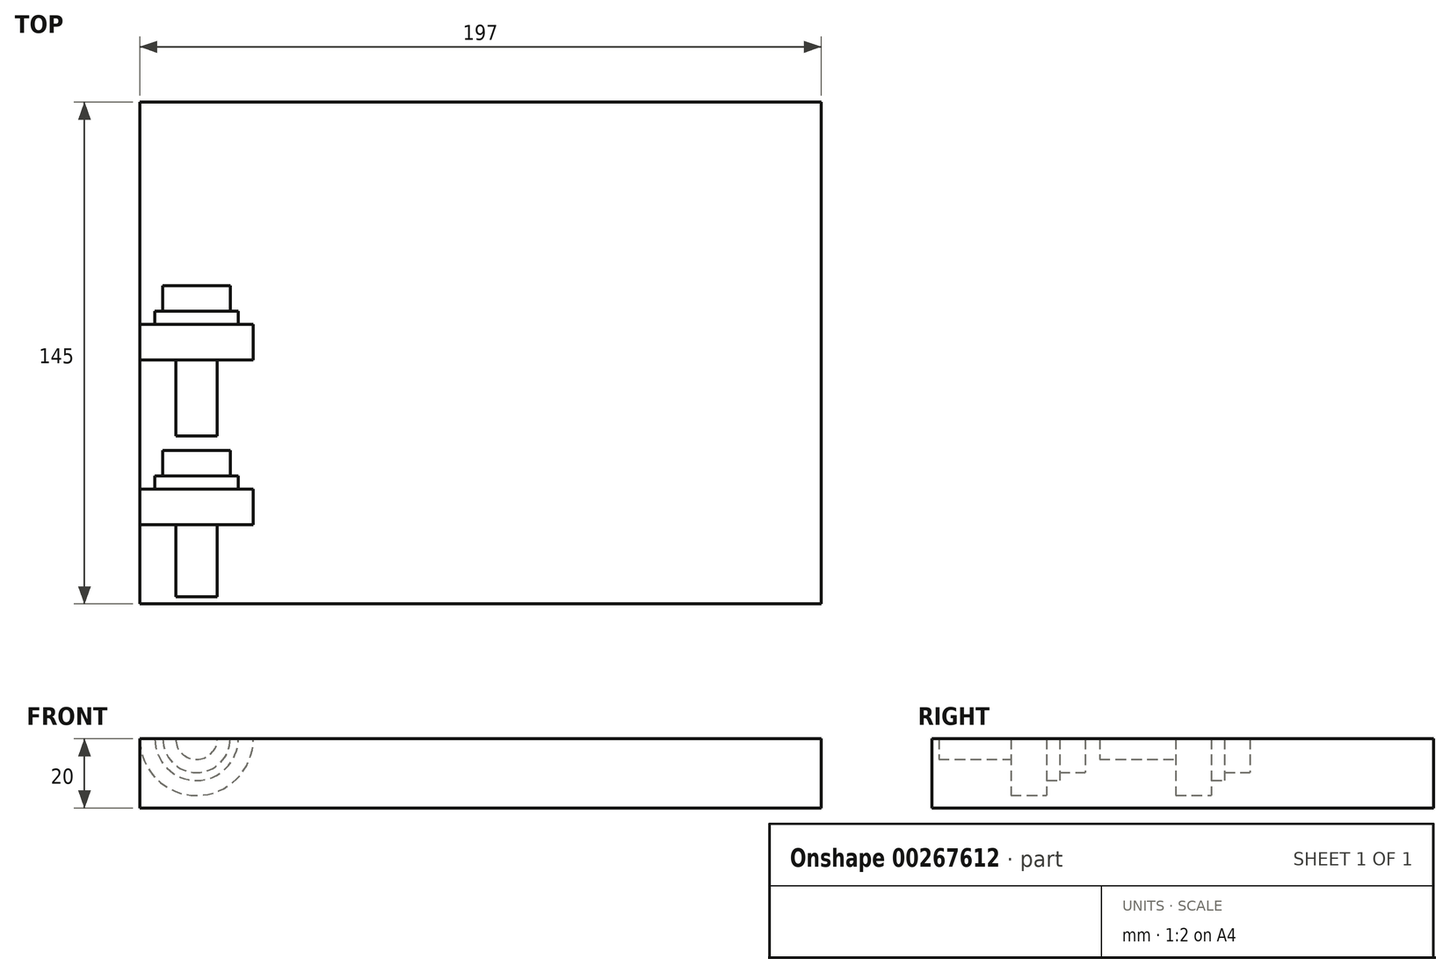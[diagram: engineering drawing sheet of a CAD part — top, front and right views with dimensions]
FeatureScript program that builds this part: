
annotation { "Feature Type Name" : "Feature", "Feature Type Description" : "" }
export const myFeature = defineFeature(function(context is Context, id is Id, definition is map)
    precondition{}
    {
        {
            var Q0;
            Q0=qCreatedBy(makeId("Top.planeOp"),FACE);
            var sketch = newSketch(context, id + "F0", { "sketchPlane" : qUnion([Q0])});
            skLineSegment(sketch, "E0.bottom", {"start": v(-40.2, 136.98) * mm, "end": v(156.8, 136.98) * mm});
            skLineSegment(sketch, "E0.top", {"start": v(-40.2, -8.02) * mm, "end": v(156.8, -8.02) * mm});
            skLineSegment(sketch, "E0.left", {"start": v(-40.2, 136.98) * mm, "end": v(-40.2, -8.02) * mm});
            skLineSegment(sketch, "E0.right", {"start": v(156.8, 136.98) * mm, "end": v(156.8, -8.02) * mm});
            skSolve(sketch);
        }
        {
            var Q0;
            Q0=makeQuery(id+"F0.imprint","IMPRINT",FACE,{"disambiguationData":[TD([[makeQuery(id+"F0.imprint","IMPRINT",EDGE,{"derivedFrom":sQuery(id+"F0.wireOp",EDGE,"E0.bottom")}),-1.0]])]});
            extrude(context, id + "F1", {"entities" : qUnion([Q0]), "depth" : 20 * mm});
        }
        {
            var Q0;
            Q0=makeQuery(id+"F1.opExtrude","CAP_FACE",FACE,{"disambiguationData":[OSD([sQuery(id+"F0.wireOp",EDGE,"E0.bottom"),sQuery(id+"F0.wireOp",EDGE,"E0.top"),sQuery(id+"F0.wireOp",EDGE,"E0.left"),sQuery(id+"F0.wireOp",EDGE,"E0.right")])],"isStart":false});
            var sketch = newSketch(context, id + "F2", { "sketchPlane" : qUnion([Q0])});
            skPoint(sketch, "E1.top.end.orphan", {"position": v(-29.8, 15.98) * mm});
            skPoint(sketch, "E2.top.start.orphan", {"position": v(-21.54, 15.98) * mm});
            skPoint(sketch, "E3.right.start.orphan", {"position": v(-38.04, 15.98) * mm});
            skLineSegment(sketch, "E4.bottom", {"start": v(-23.8, -6.02) * mm, "end": v(-29.8, -6.02) * mm});
            skLineSegment(sketch, "E4.top", {"start": v(-23.8, 14.8) * mm, "end": v(-29.8, 14.8) * mm});
            skLineSegment(sketch, "E4.left", {"start": v(-23.8, -6.02) * mm, "end": v(-23.8, 14.8) * mm});
            skLineSegment(sketch, "E4.right", {"start": v(-29.8, -6.02) * mm, "end": v(-29.8, 14.8) * mm});
            skLineSegment(sketch, "E5.bottom", {"start": v(-23.8, 14.8) * mm, "end": v(-40.2, 14.8) * mm});
            skLineSegment(sketch, "E5.top", {"start": v(-23.8, 25.1) * mm, "end": v(-40.2, 25.1) * mm});
            skLineSegment(sketch, "E5.left", {"start": v(-23.8, 14.8) * mm, "end": v(-23.8, 25.1) * mm});
            skLineSegment(sketch, "E5.right", {"start": v(-40.2, 14.8) * mm, "end": v(-40.2, 25.1) * mm});
            skLineSegment(sketch, "E6.bottom", {"start": v(-23.8, 25.1) * mm, "end": v(-35.84, 25.1) * mm});
            skLineSegment(sketch, "E6.top", {"start": v(-23.8, 28.9) * mm, "end": v(-35.84, 28.9) * mm});
            skLineSegment(sketch, "E6.left", {"start": v(-23.8, 25.1) * mm, "end": v(-23.8, 28.9) * mm});
            skLineSegment(sketch, "E6.right", {"start": v(-35.84, 25.1) * mm, "end": v(-35.84, 28.9) * mm});
            skLineSegment(sketch, "E7.bottom", {"start": v(-23.8, 28.9) * mm, "end": v(-33.54, 28.9) * mm});
            skLineSegment(sketch, "E7.top", {"start": v(-23.8, 36.3) * mm, "end": v(-33.54, 36.3) * mm});
            skLineSegment(sketch, "E7.left", {"start": v(-23.8, 28.9) * mm, "end": v(-23.8, 36.3) * mm});
            skLineSegment(sketch, "E7.right", {"start": v(-33.54, 28.9) * mm, "end": v(-33.54, 36.3) * mm});
            skLineSegment(sketch, "E8", {"start": v(-40.2, 14.8) * mm, "end": v(-40.2, 25.1) * mm, "construction": true});
            skLineSegment(sketch, "E9", {"start": v(-23.8, 88.12) * mm, "end": v(9, 88.12) * mm, "construction": true});
            skLineSegment(sketch, "E10", {"start": v(41.8, 88.12) * mm, "end": v(74.6, 88.12) * mm, "construction": true});
            skLineSegment(sketch, "E11", {"start": v(107.4, 88.12) * mm, "end": v(140.2, 88.12) * mm, "construction": true});
            skLineSegment(sketch, "E12", {"start": v(140.2, -6.02) * mm, "end": v(140.2, 40.46) * mm, "construction": true});
            skLineSegment(sketch, "E13", {"start": v(107.4, 40.46) * mm, "end": v(107.4, -6.02) * mm, "construction": true});
            skLineSegment(sketch, "E14", {"start": v(74.6, -6.02) * mm, "end": v(74.6, 40.46) * mm, "construction": true});
            skLineSegment(sketch, "E15", {"start": v(41.8, 40.46) * mm, "end": v(41.8, -6.02) * mm, "construction": true});
            skLineSegment(sketch, "E16", {"start": v(9, -6.02) * mm, "end": v(9, 40.46) * mm, "construction": true});
            skLineSegment(sketch, "E17", {"start": v(-23.8, 40.46) * mm, "end": v(-23.8, -6.02) * mm, "construction": true});
            skLineSegment(sketch, "E18", {"start": v(-23.8, 40.46) * mm, "end": v(-23.8, 89.1) * mm});
            skLineSegment(sketch, "E19", {"start": v(140.2, 40.46) * mm, "end": v(107.4, 40.46) * mm, "construction": true});
            skLineSegment(sketch, "E20", {"start": v(74.6, 40.46) * mm, "end": v(107.4, 40.46) * mm, "construction": true});
            skLineSegment(sketch, "E21", {"start": v(9, 40.46) * mm, "end": v(41.8, 40.46) * mm, "construction": true});
            skLineSegment(sketch, "E22", {"start": v(41.8, 40.46) * mm, "end": v(74.6, 40.46) * mm, "construction": true});
            skLineSegment(sketch, "E23", {"start": v(9, 40.46) * mm, "end": v(-23.8, 40.46) * mm, "construction": true});
            skLineSegment(sketch, "E24", {"start": v(-23.8, -6.02) * mm, "end": v(9, -6.02) * mm, "construction": true});
            skLineSegment(sketch, "E25", {"start": v(9, -6.02) * mm, "end": v(41.8, -6.02) * mm, "construction": true});
            skLineSegment(sketch, "E26", {"start": v(41.8, -6.02) * mm, "end": v(74.6, -6.02) * mm, "construction": true});
            skLineSegment(sketch, "E27", {"start": v(107.4, -6.02) * mm, "end": v(74.6, -6.02) * mm, "construction": true});
            skLineSegment(sketch, "E28", {"start": v(140.2, -6.02) * mm, "end": v(107.4, -6.02) * mm, "construction": true});
            skLineSegment(sketch, "E29", {"start": v(107.4, 88.12) * mm, "end": v(74.6, 88.12) * mm, "construction": true});
            skLineSegment(sketch, "E30", {"start": v(41.8, 88.12) * mm, "end": v(9, 88.12) * mm, "construction": true});
            skLineSegment(sketch, "E31", {"start": v(-23.8, 40.46) * mm, "end": v(-40.2, 40.46) * mm, "construction": true});
            skPoint(sketch, "E32.end.orphan", {"position": v(-33.54, 87.91) * mm});
            skLineSegment(sketch, "E33", {"start": v(-23.8, 40.46) * mm, "end": v(-23.8, 83.96) * mm, "construction": true});
            skLineSegment(sketch, "E34", {"start": v(-23.8, 83.96) * mm, "end": v(9, 83.96) * mm, "construction": true});
            skLineSegment(sketch, "E35", {"start": v(9, 83.96) * mm, "end": v(41.8, 83.96) * mm, "construction": true});
            skLineSegment(sketch, "E36", {"start": v(41.8, 83.96) * mm, "end": v(74.6, 83.96) * mm, "construction": true});
            skLineSegment(sketch, "E37", {"start": v(74.6, 83.96) * mm, "end": v(107.4, 83.96) * mm, "construction": true});
            skLineSegment(sketch, "E38", {"start": v(107.4, 83.96) * mm, "end": v(140.2, 83.96) * mm, "construction": true});
            skLineSegment(sketch, "E39", {"start": v(-23.8, 36.3) * mm, "end": v(9, 36.3) * mm, "construction": true});
            skLineSegment(sketch, "E40", {"start": v(9, 36.3) * mm, "end": v(41.8, 36.3) * mm, "construction": true});
            skLineSegment(sketch, "E41", {"start": v(41.8, 36.3) * mm, "end": v(74.6, 36.3) * mm, "construction": true});
            skLineSegment(sketch, "E42", {"start": v(74.6, 36.3) * mm, "end": v(107.4, 36.3) * mm, "construction": true});
            skLineSegment(sketch, "E43", {"start": v(107.4, 36.3) * mm, "end": v(140.2, 36.3) * mm, "construction": true});
            skLineSegment(sketch, "E44", {"start": v(-23.8, 40.46) * mm, "end": v(-23.8, 83.96) * mm});
            skLineSegment(sketch, "E45", {"start": v(-33.54, 83.96) * mm, "end": v(-23.8, 83.96) * mm});
            skLineSegment(sketch, "E46", {"start": v(-33.54, 83.96) * mm, "end": v(-33.54, 76.56) * mm});
            skLineSegment(sketch, "E47", {"start": v(-33.54, 76.56) * mm, "end": v(-35.84, 76.56) * mm});
            skLineSegment(sketch, "E48", {"start": v(-35.84, 76.56) * mm, "end": v(-35.84, 72.76) * mm});
            skLineSegment(sketch, "E49", {"start": v(-35.84, 72.76) * mm, "end": v(-40.2, 72.76) * mm});
            skLineSegment(sketch, "E50", {"start": v(-40.2, 72.76) * mm, "end": v(-40.2, 62.46) * mm});
            skLineSegment(sketch, "E51", {"start": v(-40.2, 62.46) * mm, "end": v(-29.8, 62.46) * mm});
            skLineSegment(sketch, "E52", {"start": v(-29.8, 62.46) * mm, "end": v(-29.8, 40.46) * mm});
            skLineSegment(sketch, "E53", {"start": v(-29.8, 40.46) * mm, "end": v(-23.8, 40.46) * mm});
            skSolve(sketch);
        }
        {
            var Q0;
            Q0 = qSketchRegion(id + "F2", true);
            var Q1;
            Q1=sQuery(id+"F2.wireOp",EDGE,"E5.left");
            revolve(context, id + "F3", {"operationType" : NewBodyOperationType.REMOVE, "entities" : qUnion([Q0]), "axis" : qUnion([Q1]), "revolveType" : RevolveType.FULL, "oppositeDirection" : true});
        }
    });
